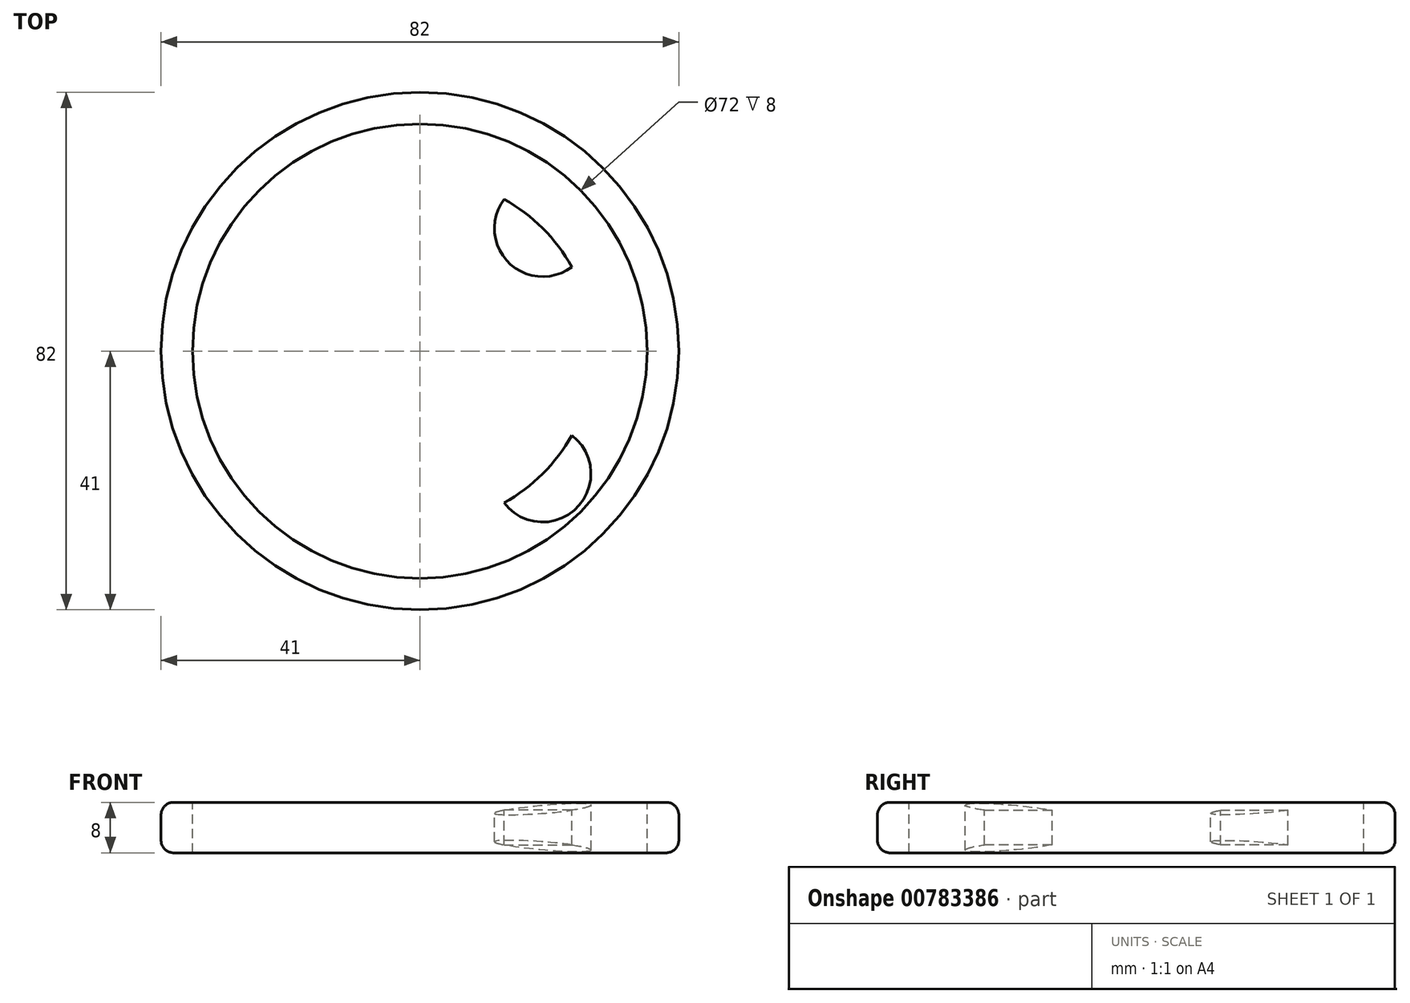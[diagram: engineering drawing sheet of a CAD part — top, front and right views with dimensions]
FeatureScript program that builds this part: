
annotation { "Feature Type Name" : "Feature", "Feature Type Description" : "" }
export const myFeature = defineFeature(function(context is Context, id is Id, definition is map)
    precondition{}
    {
        {
            var Q0;
            Q0=qCreatedBy(makeId("Top.planeOp"),FACE);
            var sketch = newSketch(context, id + "F0", { "sketchPlane" : qUnion([Q0])});
            skCircle(sketch, "E0", {"center": v(0, 0) * mm, "radius": 41 * mm});
            skSolve(sketch);
        }
        {
            var Q0;
            Q0=makeQuery(id+"F0.imprint","IMPRINT",FACE,{"disambiguationData":[TD([[makeQuery(id+"F0.imprint","IMPRINT",EDGE,{"derivedFrom":sQuery(id+"F0.wireOp",EDGE,"E0")}),1.0]])]});
            extrude(context, id + "F1", {"entities" : qUnion([Q0]), "depth" : 8 * mm, "offsetDistance" : 25 * mm});
        }
        {
            var Q0;
            Q0=qCreatedBy(makeId("Front.planeOp"),FACE);
            var sketch = newSketch(context, id + "F2", { "sketchPlane" : qUnion([Q0])});
            skArc(sketch, "E1", {"start": v(-36, 8) * mm, "mid": v(-25.04, 6.47) * mm, "end": v(-14, 5.74) * mm});
            skLineSegment(sketch, "E2", {"start": v(-36, 8) * mm, "end": v(0, 8) * mm});
            skLineSegment(sketch, "E3", {"start": v(0, 8) * mm, "end": v(0, 6) * mm});
            skLineSegment(sketch, "E4", {"start": v(-14, 8) * mm, "end": v(-14, 5.74) * mm});
            skLineSegment(sketch, "E5", {"start": v(0, 8) * mm, "end": v(0, 0) * mm});
            skLineSegment(sketch, "E6", {"start": v(0, 4) * mm, "end": v(-35.8, 4) * mm});
            skLineSegment(sketch, "E7.MirrorCS", {"start": v(0, 0) * mm, "end": v(0, 2) * mm});
            skLineSegment(sketch, "E8.MirrorCS", {"start": v(-36, 0) * mm, "end": v(0, 0) * mm});
            skLineSegment(sketch, "E9.MirrorCS", {"start": v(-14, 0) * mm, "end": v(-14, 2.26) * mm});
            skArc(sketch, "E10.MirrorCS", {"start": v(-36, 0) * mm, "mid": v(-25.04, 1.53) * mm, "end": v(-14, 2.26) * mm});
            skSolve(sketch);
        }
        {
            var Q0;
            Q0 = qSketchRegion(id + "F2", true);
            var Q1;
            Q1=sQuery(id+"F2.wireOp",EDGE,"E5");
            revolve(context, id + "F3", {"operationType" : NewBodyOperationType.REMOVE, "surfaceOperationType" : NewSurfaceOperationType.NEW, "entities" : qUnion([Q0]), "axis" : qUnion([Q1]), "revolveType" : RevolveType.FULL, "oppositeDirection" : true});
        }
        {
            var Q0;
            Q0=makeQuery(id+"F1.opExtrude","CAP_FACE",FACE,{"disambiguationData":[OSD([sQuery(id+"F0.wireOp",EDGE,"E0")])],"isStart":false});
            var sketch = newSketch(context, id + "F4", { "sketchPlane" : qUnion([Q0])});
            skCircle(sketch, "E11", {"center": v(0, 0) * mm, "radius": 27.5 * mm});
            skCircle(sketch, "E12", {"center": v(0, -27.5) * mm, "radius": 11.15 * mm});
            skCircle(sketch, "E13", {"center": v(0, 27.5) * mm, "radius": 11.15 * mm});
            skCircle(sketch, "E14", {"center": v(27.5, 0) * mm, "radius": 11.15 * mm});
            skCircle(sketch, "E15", {"center": v(-27.5, 0) * mm, "radius": 11.15 * mm});
            skSolve(sketch);
        }
        {
            var Q0;
            {var subQ0=sQuery(id+"F4.wireOp",EDGE,"E15");var subQ1=sQuery(id+"F4.wireOp",EDGE,"E11");var subQ2=makeQuery(id+"F4.imprint","INTERSECT",VERTEX,{"disambiguationData":[OD(0.0)],"derivedFrom":[subQ1,subQ0]});Q0=makeQuery(id+"F4.imprint","IMPRINT",FACE,{"disambiguationData":[TD([[makeQuery(id+"F4.imprint","IMPRINT",EDGE,{"disambiguationData":[TD([[subQ2,-1.0]])],"derivedFrom":subQ1}),-1.0]])]});}
            var Q1;
            {var subQ0=sQuery(id+"F4.wireOp",EDGE,"E15");var subQ1=sQuery(id+"F4.wireOp",EDGE,"E11");var subQ2=makeQuery(id+"F4.imprint","INTERSECT",VERTEX,{"disambiguationData":[OD(0.0)],"derivedFrom":[subQ1,subQ0]});Q1=makeQuery(id+"F4.imprint","IMPRINT",FACE,{"disambiguationData":[TD([[makeQuery(id+"F4.imprint","IMPRINT",EDGE,{"disambiguationData":[TD([[subQ2,-1.0]])],"derivedFrom":subQ1}),1.0]])]});}
            var Q2;
            {var subQ0=sQuery(id+"F4.wireOp",EDGE,"E13");var subQ1=sQuery(id+"F4.wireOp",EDGE,"E11");var subQ2=makeQuery(id+"F4.imprint","INTERSECT",VERTEX,{"disambiguationData":[OD(0.0)],"derivedFrom":[subQ1,subQ0]});Q2=makeQuery(id+"F4.imprint","IMPRINT",FACE,{"disambiguationData":[TD([[makeQuery(id+"F4.imprint","IMPRINT",EDGE,{"disambiguationData":[TD([[subQ2,-1.0]])],"derivedFrom":subQ1}),1.0]])]});}
            var Q3;
            {var subQ0=sQuery(id+"F4.wireOp",EDGE,"E13");var subQ1=sQuery(id+"F4.wireOp",EDGE,"E11");var subQ2=makeQuery(id+"F4.imprint","INTERSECT",VERTEX,{"disambiguationData":[OD(0.0)],"derivedFrom":[subQ1,subQ0]});Q3=makeQuery(id+"F4.imprint","IMPRINT",FACE,{"disambiguationData":[TD([[makeQuery(id+"F4.imprint","IMPRINT",EDGE,{"disambiguationData":[TD([[subQ2,-1.0]])],"derivedFrom":subQ1}),-1.0]])]});}
            var Q4;
            {var subQ0=sQuery(id+"F4.wireOp",EDGE,"E14");var subQ1=sQuery(id+"F4.wireOp",EDGE,"E11");var subQ2=makeQuery(id+"F4.imprint","INTERSECT",VERTEX,{"disambiguationData":[OD(0.0)],"derivedFrom":[subQ1,subQ0]});Q4=makeQuery(id+"F4.imprint","IMPRINT",FACE,{"disambiguationData":[TD([[makeQuery(id+"F4.imprint","IMPRINT",EDGE,{"disambiguationData":[TD([[subQ2,1.0]])],"derivedFrom":subQ1}),1.0]])]});}
            var Q5;
            {var subQ0=sQuery(id+"F4.wireOp",EDGE,"E14");var subQ1=sQuery(id+"F4.wireOp",EDGE,"E11");var subQ2=makeQuery(id+"F4.imprint","INTERSECT",VERTEX,{"disambiguationData":[OD(0.0)],"derivedFrom":[subQ1,subQ0]});Q5=makeQuery(id+"F4.imprint","IMPRINT",FACE,{"disambiguationData":[TD([[makeQuery(id+"F4.imprint","IMPRINT",EDGE,{"disambiguationData":[TD([[subQ2,1.0]])],"derivedFrom":subQ1}),-1.0]])]});}
            var Q6;
            {var subQ0=sQuery(id+"F4.wireOp",EDGE,"E12");var subQ1=sQuery(id+"F4.wireOp",EDGE,"E11");var subQ2=makeQuery(id+"F4.imprint","INTERSECT",VERTEX,{"disambiguationData":[OD(0.0)],"derivedFrom":[subQ1,subQ0]});Q6=makeQuery(id+"F4.imprint","IMPRINT",FACE,{"disambiguationData":[TD([[makeQuery(id+"F4.imprint","IMPRINT",EDGE,{"disambiguationData":[TD([[subQ2,-1.0]])],"derivedFrom":subQ1}),1.0]])]});}
            var Q7;
            {var subQ0=sQuery(id+"F4.wireOp",EDGE,"E12");var subQ1=sQuery(id+"F4.wireOp",EDGE,"E11");var subQ2=makeQuery(id+"F4.imprint","INTERSECT",VERTEX,{"disambiguationData":[OD(0.0)],"derivedFrom":[subQ1,subQ0]});Q7=makeQuery(id+"F4.imprint","IMPRINT",FACE,{"disambiguationData":[TD([[makeQuery(id+"F4.imprint","IMPRINT",EDGE,{"disambiguationData":[TD([[subQ2,-1.0]])],"derivedFrom":subQ1}),-1.0]])]});}
            var Q8;
            {var subQ0=sQuery(id+"F4.wireOp",EDGE,"E15");var subQ1=makeQuery(id+"F3.boolean.opBoolean","COPY",EDGE,{"derivedFrom":makeQuery(id+"F3.opRevolve","SWEPT_EDGE",EDGE,{"disambiguationData":[OSD([sQuery(id+"F2.wireOp",EDGE,"E1"),sQuery(id+"F2.wireOp",EDGE,"E2")])]})});var subQ2=makeQuery(id+"F4.imprint","INTERSECT",VERTEX,{"disambiguationData":[OD(0.0)],"derivedFrom":[subQ1,subQ0]});Q8=makeQuery(id+"F4.imprint","IMPRINT",FACE,{"disambiguationData":[TD([[makeQuery(id+"F4.imprint","IMPRINT",EDGE,{"disambiguationData":[TD([[subQ2,-1.0]])],"derivedFrom":subQ0}),1.0]])]});}
            var Q9;
            {var subQ0=sQuery(id+"F4.wireOp",EDGE,"E13");var subQ1=makeQuery(id+"F3.boolean.opBoolean","COPY",EDGE,{"derivedFrom":makeQuery(id+"F3.opRevolve","SWEPT_EDGE",EDGE,{"disambiguationData":[OSD([sQuery(id+"F2.wireOp",EDGE,"E1"),sQuery(id+"F2.wireOp",EDGE,"E2")])]})});var subQ2=makeQuery(id+"F4.imprint","INTERSECT",VERTEX,{"disambiguationData":[OD(0.0)],"derivedFrom":[subQ1,subQ0]});Q9=makeQuery(id+"F4.imprint","IMPRINT",FACE,{"disambiguationData":[TD([[makeQuery(id+"F4.imprint","IMPRINT",EDGE,{"disambiguationData":[TD([[subQ2,1.0]])],"derivedFrom":subQ0}),1.0]])]});}
            var Q10;
            {var subQ0=sQuery(id+"F4.wireOp",EDGE,"E14");var subQ1=makeQuery(id+"F3.boolean.opBoolean","COPY",EDGE,{"derivedFrom":makeQuery(id+"F3.opRevolve","SWEPT_EDGE",EDGE,{"disambiguationData":[OSD([sQuery(id+"F2.wireOp",EDGE,"E1"),sQuery(id+"F2.wireOp",EDGE,"E2")])]})});var subQ2=makeQuery(id+"F4.imprint","INTERSECT",VERTEX,{"disambiguationData":[OD(0.0)],"derivedFrom":[subQ1,subQ0]});Q10=makeQuery(id+"F4.imprint","IMPRINT",FACE,{"disambiguationData":[TD([[makeQuery(id+"F4.imprint","IMPRINT",EDGE,{"disambiguationData":[TD([[subQ2,1.0]])],"derivedFrom":subQ0}),1.0]])]});}
            var Q11;
            {var subQ0=sQuery(id+"F4.wireOp",EDGE,"E12");var subQ1=makeQuery(id+"F3.boolean.opBoolean","COPY",EDGE,{"derivedFrom":makeQuery(id+"F3.opRevolve","SWEPT_EDGE",EDGE,{"disambiguationData":[OSD([sQuery(id+"F2.wireOp",EDGE,"E1"),sQuery(id+"F2.wireOp",EDGE,"E2")])]})});var subQ2=makeQuery(id+"F4.imprint","INTERSECT",VERTEX,{"disambiguationData":[OD(0.0)],"derivedFrom":[subQ1,subQ0]});Q11=makeQuery(id+"F4.imprint","IMPRINT",FACE,{"disambiguationData":[TD([[makeQuery(id+"F4.imprint","IMPRINT",EDGE,{"disambiguationData":[TD([[subQ2,-1.0]])],"derivedFrom":subQ0}),1.0]])]});}
            extrude(context, id + "F5", {"entities" : qUnion([Q0, Q1, Q2, Q3, Q4, Q5, Q6, Q7, Q8, Q9, Q10, Q11]), "operationType" : NewBodyOperationType.REMOVE, "endBound" : BoundingType.THROUGH_ALL, "oppositeDirection" : true, "depth" : 25 * mm, "offsetDistance" : 25 * mm});
        }
        {
            var Q0;
            Q0=makeQuery(id+"F1.opExtrude","CAP_EDGE",EDGE,{"disambiguationData":[OSD([sQuery(id+"F0.wireOp",EDGE,"E0")])],"isStart":false});
            var Q1;
            Q1=makeQuery(id+"F1.opExtrude","CAP_EDGE",EDGE,{"disambiguationData":[OSD([sQuery(id+"F0.wireOp",EDGE,"E0")])],"isStart":true});
            fillet(context, id + "F6", {"entities" : qUnion([Q0, Q1]), "radius" : 2 * mm, "tangentPropagation" : true, "allowEdgeOverflow" : false});
        }
        {
            var Q0;
            Q0=makeQuery(id+"F1.opExtrude","CAP_FACE",FACE,{"disambiguationData":[OSD([sQuery(id+"F0.wireOp",EDGE,"E0")])],"isStart":false});
            var sketch = newSketch(context, id + "F7", { "sketchPlane" : qUnion([Q0])});
            skCircle(sketch, "E16", {"center": v(0, 0) * mm, "radius": 11.15 * mm});
            skSolve(sketch);
        }
        {
            var Q0;
            Q0=makeQuery(id+"F7.imprint","IMPRINT",FACE,{"disambiguationData":[TD([[makeQuery(id+"F7.imprint","IMPRINT",EDGE,{"derivedFrom":sQuery(id+"F7.wireOp",EDGE,"E16")}),1.0]])]});
            extrude(context, id + "F8", {"entities" : qUnion([Q0]), "operationType" : NewBodyOperationType.REMOVE, "endBound" : BoundingType.THROUGH_ALL, "oppositeDirection" : true, "depth" : 25 * mm, "offsetDistance" : 25 * mm});
        }
        {
            var Q0;
            Q0=makeQuery(id+"F1.opExtrude","CAP_FACE",FACE,{"disambiguationData":[OSD([sQuery(id+"F0.wireOp",EDGE,"E0")])],"isStart":false});
            var sketch = newSketch(context, id + "F9", { "sketchPlane" : qUnion([Q0])});
            skCircle(sketch, "E17", {"center": v(0, 0) * mm, "radius": 27.5 * mm});
            skLineSegment(sketch, "E18", {"start": v(0, 0) * mm, "end": v(-19.45, 19.45) * mm, "construction": true});
            skLineSegment(sketch, "E19", {"start": v(-27.5, 0) * mm, "end": v(0, 27.5) * mm, "construction": true});
            skCircle(sketch, "E20", {"center": v(-19.45, 19.45) * mm, "radius": 7.65 * mm});
            skCircle(sketch, "E21.1.0", {"center": v(-19.45, -19.45) * mm, "radius": 7.65 * mm});
            skCircle(sketch, "E21.2.0", {"center": v(19.45, -19.45) * mm, "radius": 7.65 * mm});
            skCircle(sketch, "E21.3.0", {"center": v(19.45, 19.45) * mm, "radius": 7.65 * mm});
            skSolve(sketch);
        }
        {
            var Q0;
            {var subQ0=sQuery(id+"F9.wireOp",EDGE,"E20");var subQ1=sQuery(id+"F9.wireOp",EDGE,"E17");var subQ2=makeQuery(id+"F9.imprint","INTERSECT",VERTEX,{"disambiguationData":[OD(0.0)],"derivedFrom":[subQ1,subQ0]});Q0=makeQuery(id+"F9.imprint","IMPRINT",FACE,{"disambiguationData":[TD([[makeQuery(id+"F9.imprint","IMPRINT",EDGE,{"disambiguationData":[TD([[subQ2,-1.0]])],"derivedFrom":subQ1}),-1.0]])]});}
            var Q1;
            {var subQ0=sQuery(id+"F9.wireOp",EDGE,"E20");var subQ1=sQuery(id+"F9.wireOp",EDGE,"E17");var subQ2=makeQuery(id+"F9.imprint","INTERSECT",VERTEX,{"disambiguationData":[OD(0.0)],"derivedFrom":[subQ1,subQ0]});Q1=makeQuery(id+"F9.imprint","IMPRINT",FACE,{"disambiguationData":[TD([[makeQuery(id+"F9.imprint","IMPRINT",EDGE,{"disambiguationData":[TD([[subQ2,-1.0]])],"derivedFrom":subQ1}),1.0]])]});}
            var Q2;
            {var subQ0=sQuery(id+"F9.wireOp",EDGE,"E21.2.0");var subQ1=sQuery(id+"F9.wireOp",EDGE,"E17");var subQ2=makeQuery(id+"F9.imprint","INTERSECT",VERTEX,{"disambiguationData":[OD(0.0)],"derivedFrom":[subQ1,subQ0]});Q2=makeQuery(id+"F9.imprint","IMPRINT",FACE,{"disambiguationData":[TD([[makeQuery(id+"F9.imprint","IMPRINT",EDGE,{"disambiguationData":[TD([[subQ2,-1.0]])],"derivedFrom":subQ1}),1.0]])]});}
            var Q3;
            {var subQ0=sQuery(id+"F9.wireOp",EDGE,"E21.2.0");var subQ1=sQuery(id+"F9.wireOp",EDGE,"E17");var subQ2=makeQuery(id+"F9.imprint","INTERSECT",VERTEX,{"disambiguationData":[OD(0.0)],"derivedFrom":[subQ1,subQ0]});Q3=makeQuery(id+"F9.imprint","IMPRINT",FACE,{"disambiguationData":[TD([[makeQuery(id+"F9.imprint","IMPRINT",EDGE,{"disambiguationData":[TD([[subQ2,-1.0]])],"derivedFrom":subQ1}),-1.0]])]});}
            var Q4;
            {var subQ0=sQuery(id+"F9.wireOp",EDGE,"E21.1.0");var subQ1=sQuery(id+"F9.wireOp",EDGE,"E17");var subQ2=makeQuery(id+"F9.imprint","INTERSECT",VERTEX,{"disambiguationData":[OD(0.0)],"derivedFrom":[subQ1,subQ0]});Q4=makeQuery(id+"F9.imprint","IMPRINT",FACE,{"disambiguationData":[TD([[makeQuery(id+"F9.imprint","IMPRINT",EDGE,{"disambiguationData":[TD([[subQ2,-1.0]])],"derivedFrom":subQ1}),-1.0]])]});}
            var Q5;
            {var subQ0=sQuery(id+"F9.wireOp",EDGE,"E21.1.0");var subQ1=sQuery(id+"F9.wireOp",EDGE,"E17");var subQ2=makeQuery(id+"F9.imprint","INTERSECT",VERTEX,{"disambiguationData":[OD(0.0)],"derivedFrom":[subQ1,subQ0]});Q5=makeQuery(id+"F9.imprint","IMPRINT",FACE,{"disambiguationData":[TD([[makeQuery(id+"F9.imprint","IMPRINT",EDGE,{"disambiguationData":[TD([[subQ2,-1.0]])],"derivedFrom":subQ1}),1.0]])]});}
            var Q6;
            {var subQ0=sQuery(id+"F9.wireOp",EDGE,"E21.3.0");var subQ1=sQuery(id+"F9.wireOp",EDGE,"E17");var subQ2=makeQuery(id+"F9.imprint","INTERSECT",VERTEX,{"disambiguationData":[OD(0.0)],"derivedFrom":[subQ1,subQ0]});Q6=makeQuery(id+"F9.imprint","IMPRINT",FACE,{"disambiguationData":[TD([[makeQuery(id+"F9.imprint","IMPRINT",EDGE,{"disambiguationData":[TD([[subQ2,1.0]])],"derivedFrom":subQ1}),-1.0]])]});}
            var Q7;
            {var subQ0=sQuery(id+"F9.wireOp",EDGE,"E21.3.0");var subQ1=sQuery(id+"F9.wireOp",EDGE,"E17");var subQ2=makeQuery(id+"F9.imprint","INTERSECT",VERTEX,{"disambiguationData":[OD(0.0)],"derivedFrom":[subQ1,subQ0]});Q7=makeQuery(id+"F9.imprint","IMPRINT",FACE,{"disambiguationData":[TD([[makeQuery(id+"F9.imprint","IMPRINT",EDGE,{"disambiguationData":[TD([[subQ2,1.0]])],"derivedFrom":subQ1}),1.0]])]});}
            var Q8;
            {var subQ0=sQuery(id+"F9.wireOp",EDGE,"E21.3.0");var subQ1=sQuery(id+"F2.wireOp",EDGE,"E1");var subQ2=makeQuery(id+"F5.boolean.opBoolean","SPLIT",EDGE,{"disambiguationData":[TD([makeQuery(id+"F1.opExtrude","CAP_FACE",FACE,{"disambiguationData":[OSD([sQuery(id+"F0.wireOp",EDGE,"E0")])],"isStart":false}),makeQuery(id+"F3.boolean.opBoolean","COPY",FACE,{"derivedFrom":makeQuery(id+"F3.opRevolve","SWEPT_FACE",FACE,{"disambiguationData":[OSD([subQ1])]})}),makeQuery(id+"F5.opExtrude","SWEPT_FACE",FACE,{"disambiguationData":[OSD([sQuery(id+"F4.wireOp",EDGE,"E13")])]}),makeQuery(id+"F5.opExtrude","SWEPT_FACE",FACE,{"disambiguationData":[OSD([sQuery(id+"F4.wireOp",EDGE,"E14")])]})])],"derivedFrom":makeQuery(id+"F3.boolean.opBoolean","COPY",EDGE,{"derivedFrom":makeQuery(id+"F3.opRevolve","SWEPT_EDGE",EDGE,{"disambiguationData":[OSD([subQ1,sQuery(id+"F2.wireOp",EDGE,"E2")])]})})});var subQ3=makeQuery(id+"F9.imprint","INTERSECT",VERTEX,{"disambiguationData":[OD(0.0)],"derivedFrom":[subQ2,subQ0]});Q8=makeQuery(id+"F9.imprint","IMPRINT",FACE,{"disambiguationData":[TD([[makeQuery(id+"F9.imprint","IMPRINT",EDGE,{"disambiguationData":[TD([[subQ3,-1.0]])],"derivedFrom":subQ0}),1.0]])]});}
            var Q9;
            {var subQ0=sQuery(id+"F9.wireOp",EDGE,"E21.2.0");var subQ1=sQuery(id+"F2.wireOp",EDGE,"E1");var subQ2=makeQuery(id+"F5.boolean.opBoolean","SPLIT",EDGE,{"disambiguationData":[TD([makeQuery(id+"F1.opExtrude","CAP_FACE",FACE,{"disambiguationData":[OSD([sQuery(id+"F0.wireOp",EDGE,"E0")])],"isStart":false}),makeQuery(id+"F3.boolean.opBoolean","COPY",FACE,{"derivedFrom":makeQuery(id+"F3.opRevolve","SWEPT_FACE",FACE,{"disambiguationData":[OSD([subQ1])]})}),makeQuery(id+"F5.opExtrude","SWEPT_FACE",FACE,{"disambiguationData":[OSD([sQuery(id+"F4.wireOp",EDGE,"E12")])]}),makeQuery(id+"F5.opExtrude","SWEPT_FACE",FACE,{"disambiguationData":[OSD([sQuery(id+"F4.wireOp",EDGE,"E14")])]})])],"derivedFrom":makeQuery(id+"F3.boolean.opBoolean","COPY",EDGE,{"derivedFrom":makeQuery(id+"F3.opRevolve","SWEPT_EDGE",EDGE,{"disambiguationData":[OSD([subQ1,sQuery(id+"F2.wireOp",EDGE,"E2")])]})})});var subQ3=makeQuery(id+"F9.imprint","INTERSECT",VERTEX,{"disambiguationData":[OD(0.0)],"derivedFrom":[subQ2,subQ0]});Q9=makeQuery(id+"F9.imprint","IMPRINT",FACE,{"disambiguationData":[TD([[makeQuery(id+"F9.imprint","IMPRINT",EDGE,{"disambiguationData":[TD([[subQ3,-1.0]])],"derivedFrom":subQ0}),1.0]])]});}
            var Q10;
            {var subQ0=sQuery(id+"F9.wireOp",EDGE,"E21.1.0");var subQ1=sQuery(id+"F2.wireOp",EDGE,"E1");var subQ2=makeQuery(id+"F5.boolean.opBoolean","SPLIT",EDGE,{"disambiguationData":[TD([makeQuery(id+"F1.opExtrude","CAP_FACE",FACE,{"disambiguationData":[OSD([sQuery(id+"F0.wireOp",EDGE,"E0")])],"isStart":false}),makeQuery(id+"F3.boolean.opBoolean","COPY",FACE,{"derivedFrom":makeQuery(id+"F3.opRevolve","SWEPT_FACE",FACE,{"disambiguationData":[OSD([subQ1])]})}),makeQuery(id+"F5.opExtrude","SWEPT_FACE",FACE,{"disambiguationData":[OSD([sQuery(id+"F4.wireOp",EDGE,"E12")])]}),makeQuery(id+"F5.opExtrude","SWEPT_FACE",FACE,{"disambiguationData":[OSD([sQuery(id+"F4.wireOp",EDGE,"E15")])]})])],"derivedFrom":makeQuery(id+"F3.boolean.opBoolean","COPY",EDGE,{"derivedFrom":makeQuery(id+"F3.opRevolve","SWEPT_EDGE",EDGE,{"disambiguationData":[OSD([subQ1,sQuery(id+"F2.wireOp",EDGE,"E2")])]})})});var subQ3=makeQuery(id+"F9.imprint","INTERSECT",VERTEX,{"disambiguationData":[OD(0.0)],"derivedFrom":[subQ2,subQ0]});Q10=makeQuery(id+"F9.imprint","IMPRINT",FACE,{"disambiguationData":[TD([[makeQuery(id+"F9.imprint","IMPRINT",EDGE,{"disambiguationData":[TD([[subQ3,-1.0]])],"derivedFrom":subQ0}),1.0]])]});}
            var Q11;
            {var subQ0=sQuery(id+"F9.wireOp",EDGE,"E20");var subQ1=sQuery(id+"F2.wireOp",EDGE,"E1");var subQ2=makeQuery(id+"F5.boolean.opBoolean","SPLIT",EDGE,{"disambiguationData":[TD([makeQuery(id+"F1.opExtrude","CAP_FACE",FACE,{"disambiguationData":[OSD([sQuery(id+"F0.wireOp",EDGE,"E0")])],"isStart":false}),makeQuery(id+"F3.boolean.opBoolean","COPY",FACE,{"derivedFrom":makeQuery(id+"F3.opRevolve","SWEPT_FACE",FACE,{"disambiguationData":[OSD([subQ1])]})}),makeQuery(id+"F5.opExtrude","SWEPT_FACE",FACE,{"disambiguationData":[OSD([sQuery(id+"F4.wireOp",EDGE,"E13")])]}),makeQuery(id+"F5.opExtrude","SWEPT_FACE",FACE,{"disambiguationData":[OSD([sQuery(id+"F4.wireOp",EDGE,"E15")])]})])],"derivedFrom":makeQuery(id+"F3.boolean.opBoolean","COPY",EDGE,{"derivedFrom":makeQuery(id+"F3.opRevolve","SWEPT_EDGE",EDGE,{"disambiguationData":[OSD([subQ1,sQuery(id+"F2.wireOp",EDGE,"E2")])]})})});var subQ3=makeQuery(id+"F9.imprint","INTERSECT",VERTEX,{"disambiguationData":[OD(0.0)],"derivedFrom":[subQ2,subQ0]});Q11=makeQuery(id+"F9.imprint","IMPRINT",FACE,{"disambiguationData":[TD([[makeQuery(id+"F9.imprint","IMPRINT",EDGE,{"disambiguationData":[TD([[subQ3,-1.0]])],"derivedFrom":subQ0}),1.0]])]});}
            extrude(context, id + "F10", {"entities" : qUnion([Q0, Q1, Q2, Q3, Q4, Q5, Q6, Q7, Q8, Q9, Q10, Q11]), "operationType" : NewBodyOperationType.REMOVE, "endBound" : BoundingType.THROUGH_ALL, "oppositeDirection" : true, "depth" : 25 * mm, "offsetDistance" : 25 * mm});
        }
    });
